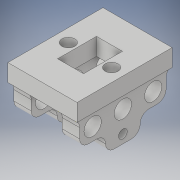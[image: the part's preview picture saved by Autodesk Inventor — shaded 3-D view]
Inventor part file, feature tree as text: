
AUTODESK INVENTOR PART (.ipt)
format: ipt  version: 2019 (Build 230136000, 136)  size: 252,928 bytes
history: native  units: mm
features: extrude x8, sketch x8, fillet x4, hole x1
ambient origin geometry x8: Origin, YZ Plane, XZ Plane, XY Plane, X Axis, Y Axis, Z Axis, Center Point
bodies: Solid1 (feature_tree)
feature tree (21):
  extrude  "Extrusion1"  Depth=80.0mm
  extrude  "Extrusion2"  Depth=30.0mm
  hole  "Hole1"  [1 undecoded]
  extrude  "Extrusion3"  Depth=20.0mm
  fillet  "Fillet1"  Radius=2.0mm
  fillet  "Fillet3"  Radius=30.0mm
  extrude  "Extrusion4"  Depth=15.0mm
  sketch  "Sketch6"  dims[d20=15.0mm d21=25.0mm]
  extrude  "Extrusion6"  Depth=25.0mm
  extrude  "Extrusion7"  Depth=15.0mm TaperAngle=0.0deg
  extrude  "Extrusion8"  Depth=10.0mm
  extrude  "Extrusion9"  Depth=45.0mm
  fillet  "Fillet7"  Radius=30.0mm
  fillet  "Fillet8"  Radius=20.0mm
  sketch  "Sketch1"  dims[d0=110.0mm d1=80.0mm]
  sketch  "Sketch2"  dims[d2=20.0mm d3=0.0mm d4=30.0mm]
  sketch  "Sketch3"  dims[d5=20.0mm d6=20.0mm]
  sketch  "Sketch4"  dims[d7=2.0mm d8=20.0mm d9=2.0mm d10=30.0mm d11=0.0mm]
  sketch  "Sketch5"  dims[d12=20.0mm d13=6.0mm d14=4.0mm d15=2.0mm d16=90.0deg d17=15.0mm d18=20.594885mm d19=15.0mm]
  sketch  "Sketch7"  dims[d23=25.0mm d24=15.0mm d25=0.0mm]
  sketch  "Sketch9"  dims[d26=10.0mm d28=10.0mm d30=45.0mm d31=30.0mm d32=20.0mm d33=0.0mm d37=50.0mm d38=0.0mm d39=50.0mm d40=0.0mm d42=20.0mm d43=15.0mm d44=100.0mm d45=0.0mm d46=10.0mm d47=10.0mm d48=100.0mm d49=0.0mm d50=10.0mm d51=10.0mm d22=0.75mm]
note: 1 required parameter value undecoded (feature->parameter linkage not recoverable at this tier; creation-order binding heuristic only, values carry confidence <= 0.55)
